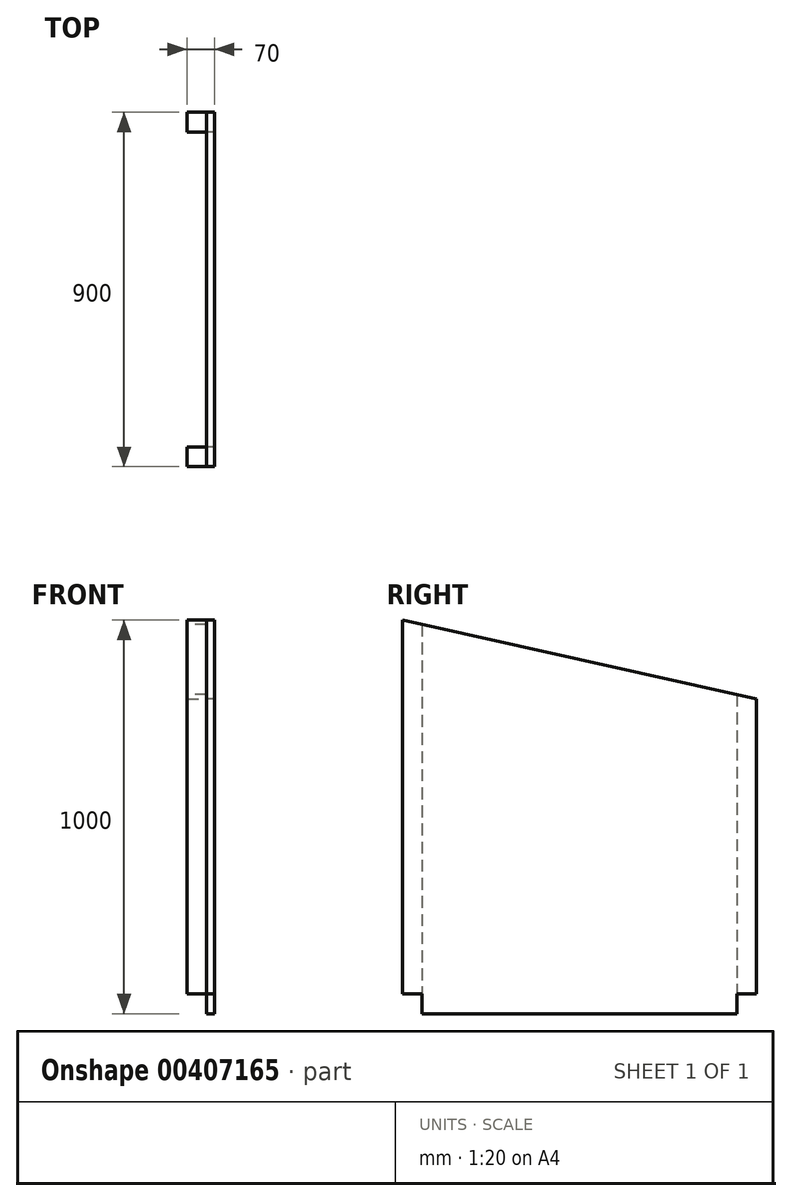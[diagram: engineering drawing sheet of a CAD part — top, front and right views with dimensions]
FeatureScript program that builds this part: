
annotation { "Feature Type Name" : "Feature", "Feature Type Description" : "" }
export const myFeature = defineFeature(function(context is Context, id is Id, definition is map)
    precondition{}
    {
        {
            var Q0;
            Q0=qCreatedBy(makeId("Right.planeOp"),FACE);
            var sketch = newSketch(context, id + "F0", { "sketchPlane" : qUnion([Q0])});
            skLineSegment(sketch, "E0", {"start": v(0, 0) * mm, "end": v(900, 0) * mm});
            skLineSegment(sketch, "E1", {"start": v(900, 0) * mm, "end": v(900, 800) * mm});
            skLineSegment(sketch, "E2", {"start": v(900, 800) * mm, "end": v(0, 1000) * mm});
            skLineSegment(sketch, "E3", {"start": v(0, 1000) * mm, "end": v(0, 0) * mm});
            skSolve(sketch);
        }
        {
            var Q0;
            Q0 = qSketchRegion(id + "F0", true);
            extrude(context, id + "F1", {"entities" : qUnion([Q0]), "depth" : 20 * mm});
        }
        {
            var Q0;
            Q0=qCreatedBy(makeId("Top.planeOp"),FACE);
            var sketch = newSketch(context, id + "F2", { "sketchPlane" : qUnion([Q0])});
            skLineSegment(sketch, "E4.bottom", {"start": v(0, 0) * mm, "end": v(-50, 0) * mm});
            skLineSegment(sketch, "E4.top", {"start": v(0, 50) * mm, "end": v(-50, 50) * mm});
            skLineSegment(sketch, "E4.left", {"start": v(0, 0) * mm, "end": v(0, 50) * mm});
            skLineSegment(sketch, "E4.right", {"start": v(-50, 0) * mm, "end": v(-50, 50) * mm});
            skSolve(sketch);
        }
        {
            var Q0;
            Q0 = qSketchRegion(id + "F2", true);
            extrude(context, id + "F3", {"entities" : qUnion([Q0]), "depth" : 1000 * mm});
        }
        {
            var Q0;
            Q0=makeQuery(id+"F1.opExtrude","CAP_FACE",FACE,{"disambiguationData":[OSD([sQuery(id+"F0.wireOp",EDGE,"E0"),sQuery(id+"F0.wireOp",EDGE,"E1"),sQuery(id+"F0.wireOp",EDGE,"E2"),sQuery(id+"F0.wireOp",EDGE,"E3")])],"isStart":false});
            var sketch = newSketch(context, id + "F4", { "sketchPlane" : qUnion([Q0])});
            skLineSegment(sketch, "E5", {"start": v(0, 1000) * mm, "end": v(140.46, 968.79) * mm});
            skLineSegment(sketch, "E6", {"start": v(140.46, 968.79) * mm, "end": v(140.46, 1058.95) * mm});
            skLineSegment(sketch, "E7", {"start": v(140.46, 1058.95) * mm, "end": v(0, 1058.95) * mm});
            skLineSegment(sketch, "E8", {"start": v(0, 1058.95) * mm, "end": v(0, 1000) * mm});
            skSolve(sketch);
        }
        {
            var Q0;
            Q0=makeQuery(id+"F4.imprint","IMPRINT",FACE,{"disambiguationData":[TD([[makeQuery(id+"F4.imprint","IMPRINT",EDGE,{"derivedFrom":sQuery(id+"F4.wireOp",EDGE,"E5")}),-1.0]])]});
            extrude(context, id + "F5", {"entities" : qUnion([Q0]), "operationType" : NewBodyOperationType.REMOVE, "oppositeDirection" : true, "depth" : 153 * mm});
        }
        {
            var Q0;
            Q0=makeQuery(id+"F3.opExtrude","SWEPT_FACE",FACE,{"disambiguationData":[OSD([sQuery(id+"F2.wireOp",EDGE,"E4.right")])]});
            var sketch = newSketch(context, id + "F6", { "sketchPlane" : qUnion([Q0])});
            skLineSegment(sketch, "E9.bottom", {"start": v(-50, 0) * mm, "end": v(0, 0) * mm});
            skLineSegment(sketch, "E9.top", {"start": v(-50, 50) * mm, "end": v(0, 50) * mm});
            skLineSegment(sketch, "E9.left", {"start": v(-50, 0) * mm, "end": v(-50, 50) * mm});
            skLineSegment(sketch, "E9.right", {"start": v(0, 0) * mm, "end": v(0, 50) * mm});
            skSolve(sketch);
        }
        {
            var Q0;
            Q0 = qSketchRegion(id + "F6", true);
            extrude(context, id + "F7", {"entities" : qUnion([Q0]), "operationType" : NewBodyOperationType.REMOVE, "oppositeDirection" : true, "depth" : 112 * mm});
        }
        {
            var Q0;
            Q0=makeQuery(id+"F1.opExtrude","SWEPT_FACE",FACE,{"disambiguationData":[OSD([sQuery(id+"F0.wireOp",EDGE,"E0")])]});
            var sketch = newSketch(context, id + "F8", { "sketchPlane" : qUnion([Q0])});
            skLineSegment(sketch, "E10.bottom", {"start": v(0, -900) * mm, "end": v(-50, -900) * mm});
            skLineSegment(sketch, "E10.top", {"start": v(0, -850) * mm, "end": v(-50, -850) * mm});
            skLineSegment(sketch, "E10.left", {"start": v(0, -900) * mm, "end": v(0, -850) * mm});
            skLineSegment(sketch, "E10.right", {"start": v(-50, -900) * mm, "end": v(-50, -850) * mm});
            skSolve(sketch);
        }
        {
            var Q0;
            Q0 = qSketchRegion(id + "F8", true);
            extrude(context, id + "F9", {"entities" : qUnion([Q0]), "oppositeDirection" : true, "depth" : 850 * mm});
        }
        {
            var Q0;
            Q0=makeQuery(id+"F1.opExtrude","CAP_FACE",FACE,{"disambiguationData":[OSD([sQuery(id+"F0.wireOp",EDGE,"E0"),sQuery(id+"F0.wireOp",EDGE,"E1"),sQuery(id+"F0.wireOp",EDGE,"E2"),sQuery(id+"F0.wireOp",EDGE,"E3")])],"isStart":false});
            var sketch = newSketch(context, id + "F10", { "sketchPlane" : qUnion([Q0])});
            skLineSegment(sketch, "E11", {"start": v(787.2, 825.07) * mm, "end": v(900, 800) * mm});
            skLineSegment(sketch, "E12", {"start": v(900, 800) * mm, "end": v(900, 899.95) * mm});
            skLineSegment(sketch, "E13", {"start": v(900, 899.95) * mm, "end": v(787.2, 899.95) * mm});
            skLineSegment(sketch, "E14", {"start": v(787.2, 899.95) * mm, "end": v(787.2, 825.07) * mm});
            skSolve(sketch);
        }
        {
            var Q0;
            Q0 = qSketchRegion(id + "F10", true);
            extrude(context, id + "F11", {"entities" : qUnion([Q0]), "operationType" : NewBodyOperationType.REMOVE, "oppositeDirection" : true, "depth" : 169 * mm});
        }
        {
            var Q0;
            Q0=makeQuery(id+"F9.opExtrude","SWEPT_FACE",FACE,{"disambiguationData":[OSD([sQuery(id+"F8.wireOp",EDGE,"E10.right")])]});
            var sketch = newSketch(context, id + "F12", { "sketchPlane" : qUnion([Q0])});
            skLineSegment(sketch, "E15.bottom", {"start": v(-900, 0) * mm, "end": v(-850, 0) * mm});
            skLineSegment(sketch, "E15.top", {"start": v(-900, 50) * mm, "end": v(-850, 50) * mm});
            skLineSegment(sketch, "E15.left", {"start": v(-900, 0) * mm, "end": v(-900, 50) * mm});
            skLineSegment(sketch, "E15.right", {"start": v(-850, 0) * mm, "end": v(-850, 50) * mm});
            skSolve(sketch);
        }
        {
            var Q0;
            Q0 = qSketchRegion(id + "F12", true);
            extrude(context, id + "F13", {"entities" : qUnion([Q0]), "operationType" : NewBodyOperationType.REMOVE, "oppositeDirection" : true, "depth" : 94 * mm});
        }
    });
